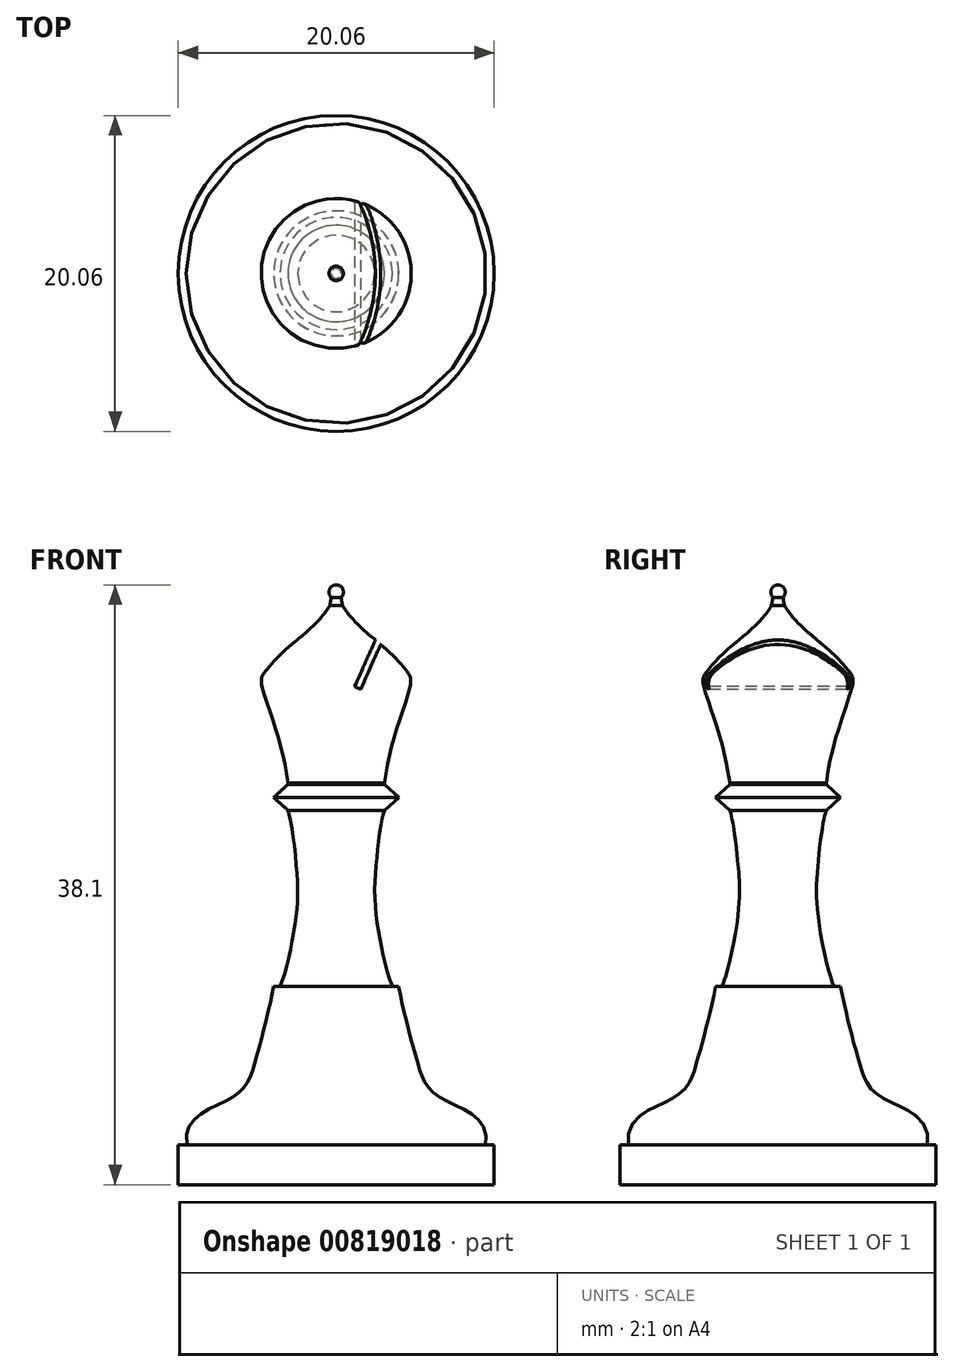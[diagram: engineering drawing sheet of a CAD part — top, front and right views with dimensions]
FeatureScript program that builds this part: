
annotation { "Feature Type Name" : "Feature", "Feature Type Description" : "" }
export const myFeature = defineFeature(function(context is Context, id is Id, definition is map)
    precondition{}
    {
        {
            var Q0;
            Q0=qCreatedBy(makeId("Front.planeOp"),FACE);
            var sketch = newSketch(context, id + "F0", { "sketchPlane" : qUnion([Q0])});
            skLineSegment(sketch, "E0", {"start": v(0, 0) * mm, "end": v(10.03, 0) * mm});
            skLineSegment(sketch, "E1", {"start": v(0, 0) * mm, "end": v(0, 38.1) * mm});
            skLineSegment(sketch, "E2", {"start": v(10.03, 0) * mm, "end": v(10.03, 2.54) * mm});
            skLineSegment(sketch, "E3", {"start": v(10.03, 2.54) * mm, "end": v(0, 2.54) * mm});
            skFitSpline(sketch, "E4", {"points": [v(9.49, 2.54) * mm, v(6.53, 5.59) * mm, v(5.14, 7.84) * mm, v(3.96, 12.6) * mm], "startDerivative": vector(3.09, 16.22) * mm, "endDerivative": vector(-2.05, 11.03) * mm});
            skLineSegment(sketch, "E5", {"start": v(3.96, 12.6) * mm, "end": v(3.56, 12.6) * mm});
            skFitSpline(sketch, "E6", {"points": [v(3.56, 12.6) * mm, v(2.62, 16.53) * mm, v(2.5, 19.83) * mm, v(3.06, 23.78) * mm], "startDerivative": vector(-3.13, 6.27) * mm, "endDerivative": vector(1.88, 4.75) * mm});
            skLineSegment(sketch, "E7", {"start": v(3.06, 23.78) * mm, "end": v(3.97, 24.6) * mm});
            skLineSegment(sketch, "E8", {"start": v(3.97, 24.6) * mm, "end": v(3.06, 25.43) * mm});
            skLineSegment(sketch, "E9", {"start": v(3.06, 25.43) * mm, "end": v(3.06, 25.53) * mm});
            skCircle(sketch, "E10", {"center": v(0, 37.64) * mm, "radius": 0.46 * mm});
            skPoint(sketch, "E10.third.point", {"position": v(0.45, 37.74) * mm});
            skLineSegment(sketch, "E11", {"start": v(0.32, 37.3) * mm, "end": v(0.4, 36.78) * mm});
            skFitSpline(sketch, "E12", {"points": [v(3.06, 25.53) * mm, v(4.73, 31.74) * mm, v(4.62, 32.44) * mm, v(3.1, 34.08) * mm, v(0.4, 36.78) * mm], "startDerivative": vector(2.7, 21.7) * mm, "endDerivative": vector(-7.58, 12.2) * mm});
            skLineSegment(sketch, "E13", {"start": v(3.56, 37.01) * mm, "end": v(1.17, 31.64) * mm});
            skLineSegment(sketch, "E14", {"start": v(1.17, 31.64) * mm, "end": v(1.56, 31.46) * mm});
            skLineSegment(sketch, "E15", {"start": v(1.56, 31.46) * mm, "end": v(3.95, 36.86) * mm});
            skLineSegment(sketch, "E16", {"start": v(3.95, 36.86) * mm, "end": v(3.56, 37.01) * mm});
            skSolve(sketch);
        }
        {
            var Q0;
            {var subQ2=sQuery(id+"F0.wireOp",EDGE,"E0");Q0=makeQuery(id+"F0.imprint","IMPRINT",FACE,{"disambiguationData":[TD([[makeQuery(id+"F0.imprint","IMPRINT",EDGE,{"derivedFrom":subQ2}),1.0]])]});}
            var Q1;
            {var subQ4=sQuery(id+"F0.wireOp",EDGE,"E4");Q1=makeQuery(id+"F0.imprint","IMPRINT",FACE,{"disambiguationData":[TD([[makeQuery(id+"F0.imprint","IMPRINT",EDGE,{"derivedFrom":subQ4}),1.0]])]});}
            var Q2;
            {var subQ0=sQuery(id+"F0.wireOp",EDGE,"E10");var subQ1=sQuery(id+"F0.wireOp",EDGE,"E1");var subQ2=makeQuery(id+"F0.imprint","INTERSECT",VERTEX,{"derivedFrom":[subQ1,subQ0]});Q2=makeQuery(id+"F0.imprint","IMPRINT",FACE,{"disambiguationData":[TD([[makeQuery(id+"F0.imprint","IMPRINT",EDGE,{"disambiguationData":[TD([[subQ2,1.0]])],"derivedFrom":subQ1}),-1.0]])]});}
            var Q3;
            {var subQ3=sQuery(id+"F0.wireOp",EDGE,"E11");Q3=makeQuery(id+"F0.imprint","IMPRINT",FACE,{"disambiguationData":[TD([[makeQuery(id+"F0.imprint","IMPRINT",EDGE,{"derivedFrom":subQ3}),-1.0]])]});}
            var Q4;
            {var subQ5=sQuery(id+"F0.wireOp",EDGE,"E14");Q4=makeQuery(id+"F0.imprint","IMPRINT",FACE,{"disambiguationData":[TD([[makeQuery(id+"F0.imprint","IMPRINT",EDGE,{"derivedFrom":subQ5}),1.0]])]});}
            var Q5;
            Q5=sQuery(id+"F0.wireOp",EDGE,"E1");
            revolve(context, id + "F1", {"surfaceOperationType" : NewSurfaceOperationType.NEW, "entities" : qUnion([Q0, Q1, Q2, Q3, Q4]), "axis" : qUnion([Q5]), "revolveType" : RevolveType.FULL});
        }
        {
            var Q0;
            {var subQ5=sQuery(id+"F0.wireOp",EDGE,"E16");Q0=makeQuery(id+"F0.imprint","IMPRINT",FACE,{"disambiguationData":[TD([[makeQuery(id+"F0.imprint","IMPRINT",EDGE,{"derivedFrom":subQ5}),1.0]])]});}
            var Q1;
            {var subQ5=sQuery(id+"F0.wireOp",EDGE,"E14");Q1=makeQuery(id+"F0.imprint","IMPRINT",FACE,{"disambiguationData":[TD([[makeQuery(id+"F0.imprint","IMPRINT",EDGE,{"derivedFrom":subQ5}),1.0]])]});}
            extrude(context, id + "F2", {"entities" : qUnion([Q0, Q1]), "operationType" : NewBodyOperationType.REMOVE, "oppositeDirection" : true, "depth" : 25.4 * mm, "offsetDistance" : 25.4 * mm});
        }
        {
            var Q0;
            Q0=makeQuery(id+"F2.boolean.opBoolean","COPY",FACE,{"derivedFrom":makeQuery(id+"F2.opExtrude","CAP_FACE",FACE,{"disambiguationData":[OSD([sQuery(id+"F0.wireOp",EDGE,"E13"),sQuery(id+"F0.wireOp",EDGE,"E14"),sQuery(id+"F0.wireOp",EDGE,"E15"),sQuery(id+"F0.wireOp",EDGE,"E16")])],"isStart":true})});
            extrude(context, id + "F3", {"entities" : qUnion([Q0]), "operationType" : NewBodyOperationType.REMOVE, "oppositeDirection" : true, "depth" : 25.4 * mm, "offsetDistance" : 25.4 * mm});
        }
    });
